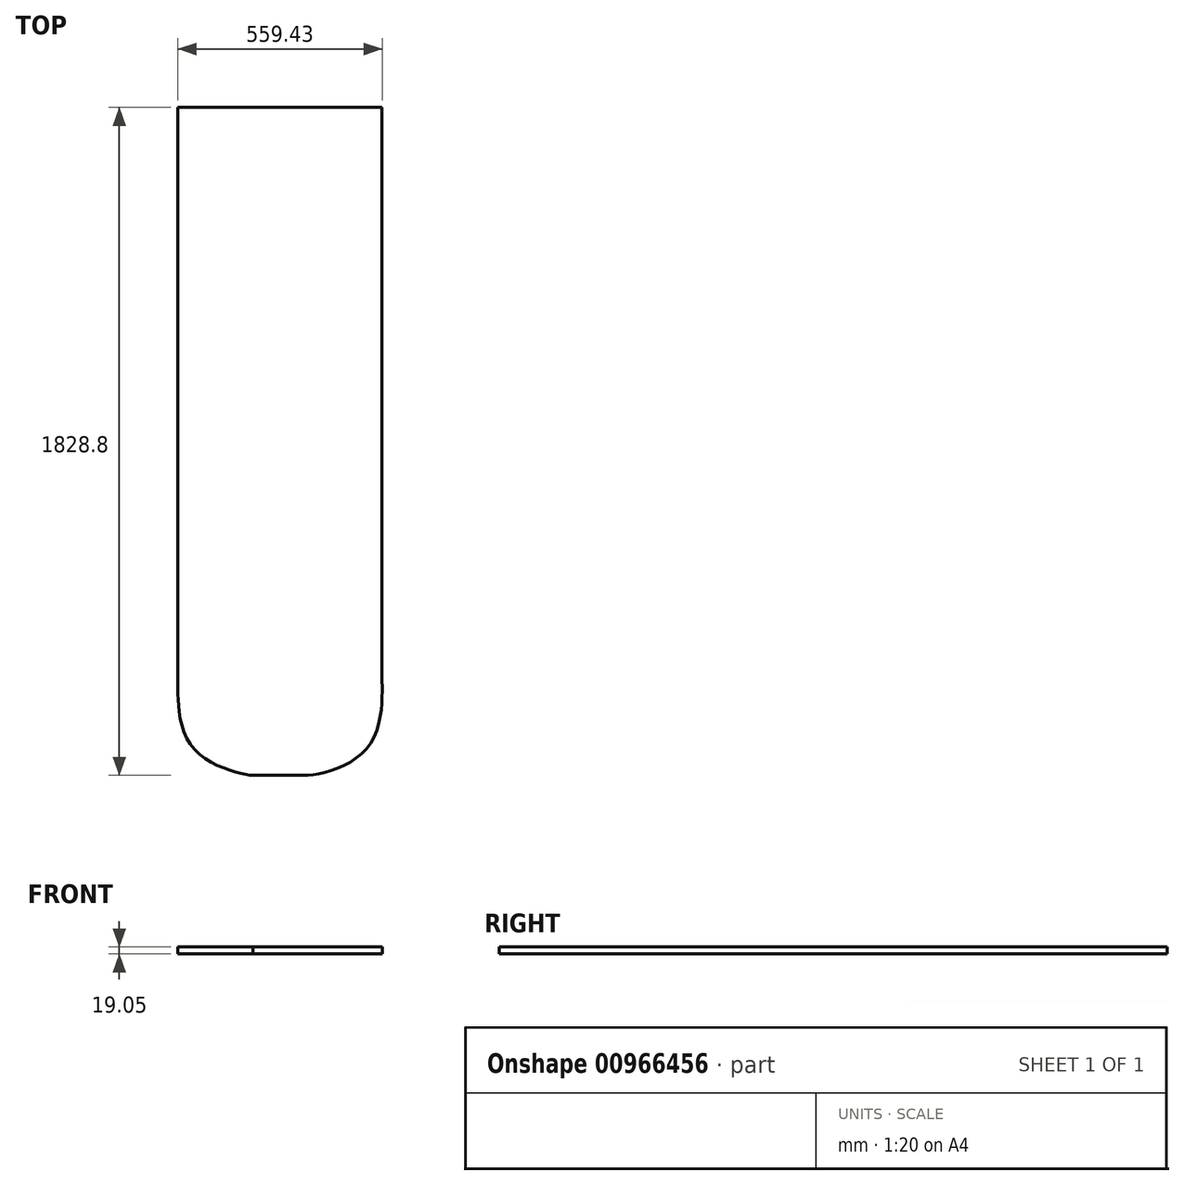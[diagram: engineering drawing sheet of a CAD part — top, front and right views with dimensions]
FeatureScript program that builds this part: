
annotation { "Feature Type Name" : "Feature", "Feature Type Description" : "" }
export const myFeature = defineFeature(function(context is Context, id is Id, definition is map)
    precondition{}
    {
        {
            var Q0;
            Q0=qCreatedBy(makeId("Top.planeOp"),FACE);
            var sketch = newSketch(context, id + "F0", { "sketchPlane" : qUnion([Q0])});
            skLineSegment(sketch, "E0.bottom", {"start": v(0, 0) * mm, "end": v(558.8, 0) * mm});
            skLineSegment(sketch, "E0.top", {"start": v(204.75, -1828.8) * mm, "end": v(345.36, -1828.8) * mm});
            skLineSegment(sketch, "E0.left", {"start": v(0, 0) * mm, "end": v(0, -1573.33) * mm});
            skLineSegment(sketch, "E0.right", {"start": v(558.8, 0) * mm, "end": v(558.8, -1563.6) * mm});
            skFitSpline(sketch, "E1", {"points": [v(345.36, -1828.8) * mm, v(523.83, -1746.53) * mm, v(558.8, -1563.6) * mm], "startDerivative": vector(240.18, 1.66) * mm, "endDerivative": vector(0.5, 175.33) * mm});
            skFitSpline(sketch, "E2", {"points": [v(0, -1573.33) * mm, v(38.5, -1749.7) * mm, v(204.75, -1828.8) * mm], "startDerivative": vector(0, -156.83) * mm, "endDerivative": vector(157.39, -10.18) * mm});
            skSolve(sketch);
        }
        {
            var Q0;
            Q0=makeQuery(id+"F0.imprint","IMPRINT",FACE,{"disambiguationData":[TD([[makeQuery(id+"F0.imprint","IMPRINT",EDGE,{"derivedFrom":sQuery(id+"F0.wireOp",EDGE,"E0.bottom")}),-1.0]])]});
            extrude(context, id + "F1", {"entities" : qUnion([Q0]), "depth" : 19.05 * mm, "offsetDistance" : 25.4 * mm});
        }
    });
